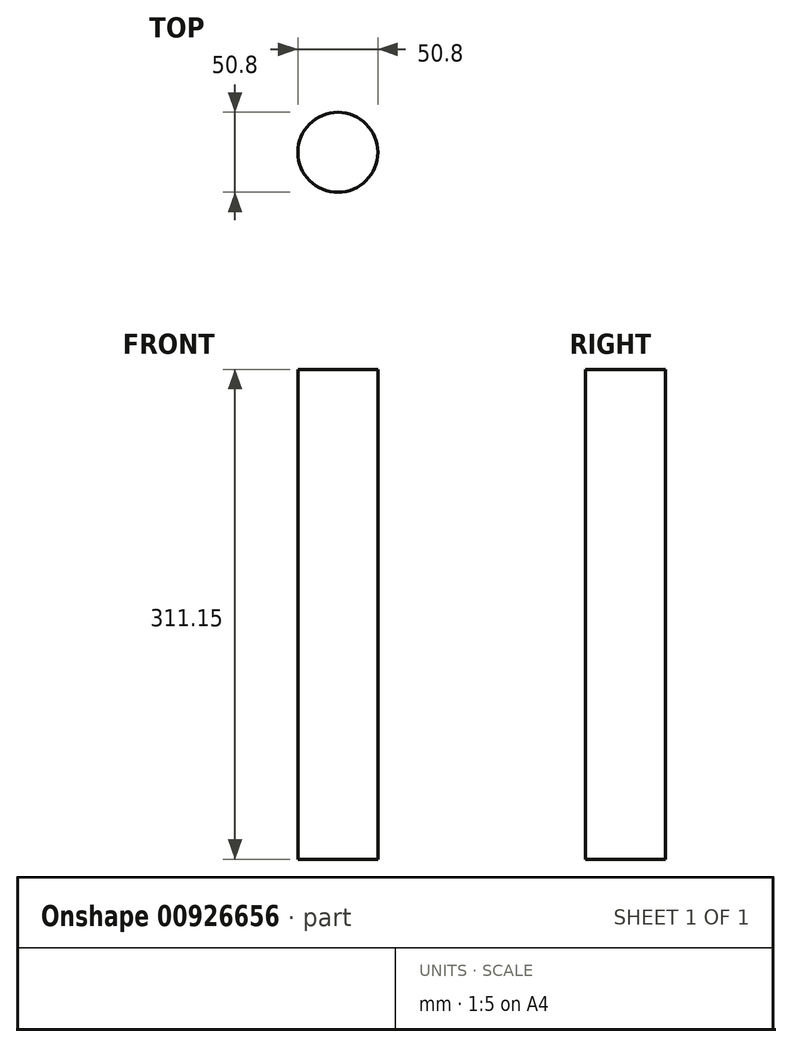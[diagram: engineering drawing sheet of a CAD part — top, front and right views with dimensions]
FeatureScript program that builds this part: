
annotation { "Feature Type Name" : "Feature", "Feature Type Description" : "" }
export const myFeature = defineFeature(function(context is Context, id is Id, definition is map)
    precondition{}
    {
        {
            var Q0;
            Q0=qCreatedBy(makeId("Top.planeOp"),FACE);
            var sketch = newSketch(context, id + "F0", { "sketchPlane" : qUnion([Q0])});
            skCircle(sketch, "E0", {"center": v(-12.81, 12.44) * mm, "radius": 25.4 * mm});
            skSolve(sketch);
        }
        {
            var Q0;
            Q0=makeQuery(id+"F0.imprint","IMPRINT",FACE,{"disambiguationData":[TD([[makeQuery(id+"F0.imprint","IMPRINT",EDGE,{"derivedFrom":sQuery(id+"F0.wireOp",EDGE,"E0")}),1.0]])]});
            extrude(context, id + "F1", {"entities" : qUnion([Q0]), "depth" : 311.15 * mm, "offsetDistance" : 25.4 * mm});
        }
    });
